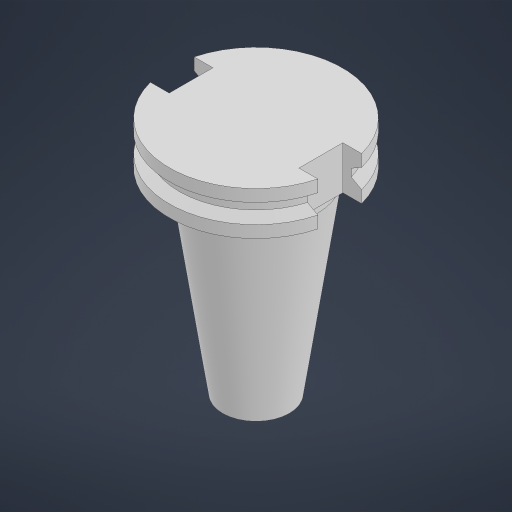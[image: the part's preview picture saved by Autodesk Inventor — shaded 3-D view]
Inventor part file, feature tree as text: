
AUTODESK INVENTOR PART (.ipt)
format: ipt  version: 2024.1 (Build 281209000, 209)  size: 233,984 bytes
history: native  units: mm
features: sketch x2, revolve x1, extrude x1, projected_geometry x1
ambient origin geometry x8: Origin, YZ Plane, XZ Plane, XY Plane, X Axis, Y Axis, Z Axis, Center Point
bodies: Solid1 (feature_tree)
feature tree (5):
  sketch  "Sketch1"  dims[d0=60.0deg d1=56.25mm]
  revolve  "Revolution1"  [1 undecoded]
  extrude  "Extrusion1"  Depth=47.65mm
  sketch  "Sketch2"  dims[d2=63.55mm d3=15.9mm d5=7.0mm d6=72.3mm d7=360.0deg d9=0.0mm d10=0.0mm d12=16.1mm d13=47.65mm d14=3.5mm d15=44.45mm d16=68.4mm d17=1.448623mm d18=25.0mm d19=16.0mm d20=24.493038mm]
  projected_geometry  "Projected Loop1"
note: 1 required parameter value undecoded (feature->parameter linkage not recoverable at this tier; creation-order binding heuristic only, values carry confidence <= 0.55)
